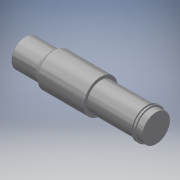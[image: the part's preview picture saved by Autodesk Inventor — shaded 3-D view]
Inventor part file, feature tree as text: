
AUTODESK INVENTOR PART (.ipt)
format: ipt  version: 2019 (Build 230136000, 136)  size: 147,968 bytes
history: native  units: mm
features: other x6, chamfer x1, fillet x1
ambient origin geometry x6: Origin, XZ Plane, XY Plane, X Axis, Y Axis, Z Axis
bodies: Body1 (feature_tree)
feature tree (8):
  other  "實體1"
  other  "迴轉1"
  chamfer  "倒角1"  [1 undecoded]
  fillet  "圓角1"  Radius=9.0mm
  other  "扣環槽1"
  other  "起始平面"
  other  "主要草圖"
  other  "iFeature27:1"
note: 1 required parameter value undecoded (feature->parameter linkage not recoverable at this tier; creation-order binding heuristic only, values carry confidence <= 0.55)
